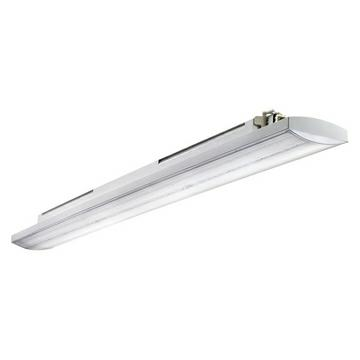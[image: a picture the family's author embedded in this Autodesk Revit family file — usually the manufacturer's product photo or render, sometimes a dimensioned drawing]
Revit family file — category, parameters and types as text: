
# Revit family: Lighting-Industriale-GEWISS-SMART[3]PLUS-HLO-PLAFONIERA-LED_TRANSPARENTE_FASCIOMEDIO_1600mm
name_source: partatom
category: Apparecchi per illuminazione
units: mm (PartAtom-declared; Revit-internal decimal feet)

## family parameters
Condiviso = No
Host = Superficie
Punto di calcolo locali = No
Quota connettore circolare = Usa diametro
Sorgente d'illuminazione = Sì
Taglio con vuoti quando caricato = No
Tipo di parte = Normale

## types (1)
- Lighting-Industriale-GEWISS-SMART[3]PLUS-HLO-PLAFONIERA-LED_TRANSPARENTE_FASCIOMEDIO_1600mm
    Angolo inclinazione = -90.00°
    Applicazione = Interno
    Carico apparente = 67 VA
    Catalogo = LIGHTING
    Catalogo Serie = SMART[3] PLUS HLO
    Classe di efficienza LED integrati = A ÷ A++
    Classe isolamento = II
    Codice Electrocod = 2434
    Commenti sul wattaggio = 67W
    Descrizione = SMART3 PLUS 1600 T.W.DALI HO CONC 9 57
    Emetti da lunghezza linea = 1200 mm
    File diagramma fotometrico = GWS3323BC957.IES
    Filtro dei colori = 16777215
    Ganci = Alluminio
    Garanzia = 5 anni
    Glow Wire Test = 850°C
    Grado di protezione = IP66/IP69
    IDF = f4548ec7-d4a7-426e-88fc-f48177b86a4a
    IDT = b00432e8-6c7e-4c0b-b2bb-cd3ca21adb70
    Immagine tipo = GWS3280TS.jpg
    Lampada = LED
    Lampada: = LED
    Lumen output (lm) = 7100
    Lunghezza = 1600 mm
    Lunghezza Lampada = 1600 mm  [stored 5.24934 ft]
    Modello = GWS3323BC957
    Numero poli = 2
    Potenza di sistema = 63 W
    Produttore = GEWISS S.p.A.
    Prospetto di default = 1219 mm
    Resistenza agli urti = IK08
    SEO = Plafoniera
    Scheda Tecnica = https://www.gewiss.com
    Schermo = Trasparente
    Schermo. = Led Acceso
    Stampa 1_100 = Sì
    Stampa 1_200 = No
    Struttura = GRIGIO
    Temperatura di colore = 5700 K (CRI > 90)
    Temperatura di colore: = 5700 K (CRI > 90)
    Temperatura di funzionamento = -25 +45 °C
    Temperatura di utilizzo = -25 +45 °C
    Tensione = 220-240 V
    Tipologia = DALI
    Tipologia sorgente luminosa = LED - Non sostituibile
    URL = https://www.gewiss.com
    Variazione temperatura colore lampada con luminosità attenuata = <Nessuno>
    Versione file RFA = 20.0

note: [stored X ft] marks values corroborated as IEEE doubles in the binary element streams (Revit-internal decimal feet)
